# Revit family: Camera-Security-iPRO-FixedDome-Outdoor-MultiSensor-4x4K-Vandal_Resistant-Weatherproof-Network-S8574SeriesX
name_source: partatom
category: Security Devices
units: mm (PartAtom-declared; Revit-internal decimal feet)

## family parameters
Cut with Voids When Loaded = No
Host = Face
Maintain Annotation Orientation = No
OmniClass Number = 23.85.10.14.11
OmniClass Title = Cameras
Part Type = Normal
Room Calculation Point = No
Round Connector Dimension = Use Diameter
Shared = No

## types (1)
- WV-S8574L
    Alarm Input Or Output = ALARM IN 1 (Alarm input 1/ Black & white input/ Auto time adjustment input) (x1), ALARM IN 2 (Alarm input 2/ ALARM OUT) (x1), ALARM IN 3 (Alarm input 3/ ALARM OUT/ AUX OUT) (x1)
    Angle Of View = 108
    Audio In = Yes
    Audio Out = Yes
    C1234 Pan Max = 30.00°
    C1234 Pan Min = -30.00°
    C1234 Tilt Max = 105.00°
    C1234 Tilt Min = 10.00°
    C1234 VV Horizontal Offset = 2.618 "
    C1234 VV Viewpoint Depth = 1.154 "
    C1234 Yaw Max = 90.00°
    C1234 Yaw Min = -90.00°
    Camera Pan Angle = 0.00°
    Camera Type = 8574
    Communication Ports = 10Base-T / 100Base-TX / 1000Base-T, RJ45 connector
    Date Last Modified = 2022/07/28
    Day Or Night = Yes
    Default Elevation = 0 "
    Description = Security Camera, Dome, Vandal Resistant, Waterproof Network, 4 x 4K Ultra HD Multi-Sensor, WV-S8574L
    Diameter = 11.811 "
    Equipment Abbreviation = SC
    Family Version = 1.0.0
    Has POE = Yes
    Height = 3.543 "
    IP Or Analog = IP
    Indoor Or Outdoor = Outdoor
    Manufacturer = i-PRO Co., Ltd.
    Minimum Illumination = 0.084 lx
    Mobile Terminal Compatibility = iPad, iPhone, Android™ terminals
    Model = WV-S8574L
    Model Disclaimer = Contact i-PRO for more information
    Mounting Positions = Mount Dependent or Surface Mount
    Operational Humidity = 10 to 100 % (no condensation)
    Operational Temperature = –40 °C to +60 °C7 {–40 °F to 140 °F}
    Panning Range for each Sensor = -30 to +30
    Part Description = Security Camera, Dome, Vandal Resistant, Waterproof Network, 4 x 4K Ultra HD Multi-Sensor, WV-S8574L
    Part Number = WV-S8574L
    Power Active = 25.4 W
    Power Supply Type = PoE+
    Product Documentation Link = https://bizpartner.panasonic.net
    Product Page URL = https://i-pro.com
    Provide Feedback = https://i-pro.com
    Regulatory Compliance = UL (UL62368-1), c-UL (CSA C22.2 No.62368-1), CE, IEC62368-1, FCC (Part15 ClassA), ICES-003 ClassA, EN55032 ClassA, EN55024
    SDXC SDHC SD Memory Card Slot = Yes
    Shock Resistance = IK10 (IEC 62262)
    Storage Temperature = –40 °C to +60 °C7 {–40 °F to 140 °F}
    Tilting Range = +10 to +105
    URL = https://i-pro.com
    Voltage = 54 V
    Water and Dust Resistance = IP67/IP66 (IEC 60529), Type 4X (UL50E), NEMA 4X compliant
    Weight = 7.28 lb
    Wide Dynamic Range = Yes
    Yawing Range for each Sensor = -90 to +90
    z Base Height = 0.591 "
    z Camera Pan Axis Length = 3.937 "
    z Camera Pan Handle Length = 7.874 "
    z Camera Tilt Handle Length = 2.756 "

## geometry (parser evidence)
native form markers: Blend x2, Sweep x16
no freeform markers — native parametric forms only
